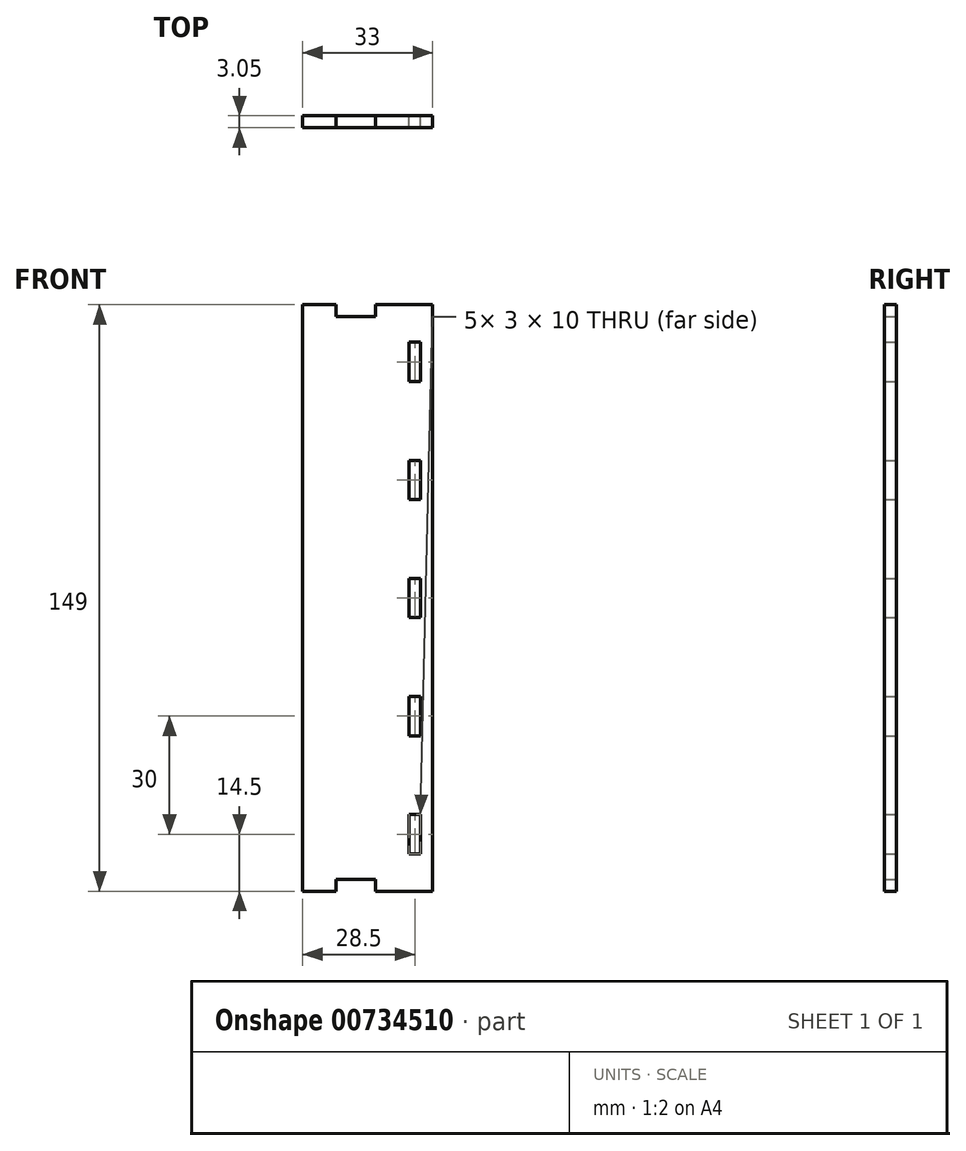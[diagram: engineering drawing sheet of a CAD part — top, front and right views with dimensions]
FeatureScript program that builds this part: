
annotation { "Feature Type Name" : "Feature", "Feature Type Description" : "" }
export const myFeature = defineFeature(function(context is Context, id is Id, definition is map)
    precondition{}
    {
        {
            var Q0;
            Q0=qCreatedBy(makeId("Front.planeOp"),FACE);
            var sketch = newSketch(context, id + "F0", { "sketchPlane" : qUnion([Q0])});
            skLineSegment(sketch, "E0", {"start": v(2, 74.5) * mm, "end": v(16.5, 74.5) * mm});
            skLineSegment(sketch, "E1", {"start": v(16.5, 74.5) * mm, "end": v(16.5, -74.5) * mm});
            skLineSegment(sketch, "E2", {"start": v(16.5, -74.5) * mm, "end": v(2, -74.5) * mm});
            skLineSegment(sketch, "E3", {"start": v(2, -74.5) * mm, "end": v(2, -71.5) * mm});
            skLineSegment(sketch, "E4", {"start": v(2, -71.5) * mm, "end": v(-8, -71.5) * mm});
            skLineSegment(sketch, "E5", {"start": v(-8, -71.5) * mm, "end": v(-8, -74.5) * mm});
            skLineSegment(sketch, "E6", {"start": v(-8, -74.5) * mm, "end": v(-16.5, -74.5) * mm});
            skLineSegment(sketch, "E7", {"start": v(-16.5, -74.5) * mm, "end": v(-16.5, 74.5) * mm});
            skLineSegment(sketch, "E8", {"start": v(-16.5, 74.5) * mm, "end": v(-8, 74.5) * mm});
            skLineSegment(sketch, "E9", {"start": v(-8, 74.5) * mm, "end": v(-8, 71.5) * mm});
            skLineSegment(sketch, "E10", {"start": v(-8, 71.5) * mm, "end": v(2, 71.5) * mm});
            skLineSegment(sketch, "E11", {"start": v(2, 71.5) * mm, "end": v(2, 74.5) * mm});
            skLineSegment(sketch, "E12", {"start": v(13.5, 65) * mm, "end": v(10.5, 65) * mm});
            skLineSegment(sketch, "E13", {"start": v(10.5, 65) * mm, "end": v(10.5, 55) * mm});
            skLineSegment(sketch, "E14", {"start": v(10.5, 55) * mm, "end": v(13.5, 55) * mm});
            skLineSegment(sketch, "E15", {"start": v(13.5, 55) * mm, "end": v(13.5, 65) * mm});
            skLineSegment(sketch, "E16", {"start": v(13.5, 35) * mm, "end": v(10.5, 35) * mm});
            skLineSegment(sketch, "E17", {"start": v(10.5, 35) * mm, "end": v(10.5, 25) * mm});
            skLineSegment(sketch, "E18", {"start": v(10.5, 25) * mm, "end": v(13.5, 25) * mm});
            skLineSegment(sketch, "E19", {"start": v(13.5, 25) * mm, "end": v(13.5, 35) * mm});
            skLineSegment(sketch, "E20", {"start": v(13.5, 5) * mm, "end": v(10.5, 5) * mm});
            skLineSegment(sketch, "E21", {"start": v(10.5, 5) * mm, "end": v(10.5, -5) * mm});
            skLineSegment(sketch, "E22", {"start": v(10.5, -5) * mm, "end": v(13.5, -5) * mm});
            skLineSegment(sketch, "E23", {"start": v(13.5, -5) * mm, "end": v(13.5, 5) * mm});
            skLineSegment(sketch, "E24", {"start": v(13.5, -25) * mm, "end": v(10.5, -25) * mm});
            skLineSegment(sketch, "E25", {"start": v(10.5, -25) * mm, "end": v(10.5, -35) * mm});
            skLineSegment(sketch, "E26", {"start": v(10.5, -35) * mm, "end": v(13.5, -35) * mm});
            skLineSegment(sketch, "E27", {"start": v(13.5, -35) * mm, "end": v(13.5, -25) * mm});
            skLineSegment(sketch, "E28", {"start": v(13.5, -55) * mm, "end": v(10.5, -55) * mm});
            skLineSegment(sketch, "E29", {"start": v(10.5, -55) * mm, "end": v(10.5, -65) * mm});
            skLineSegment(sketch, "E30", {"start": v(10.5, -65) * mm, "end": v(13.5, -65) * mm});
            skLineSegment(sketch, "E31", {"start": v(13.5, -65) * mm, "end": v(13.5, -55) * mm});
            skSolve(sketch);
        }
        {
            var Q0;
            Q0 = qSketchRegion(id + "F0", true);
            extrude(context, id + "F1", {"entities" : qUnion([Q0]), "depth" : 3.05 * mm, "offsetDistance" : 25.4 * mm});
        }
    });
